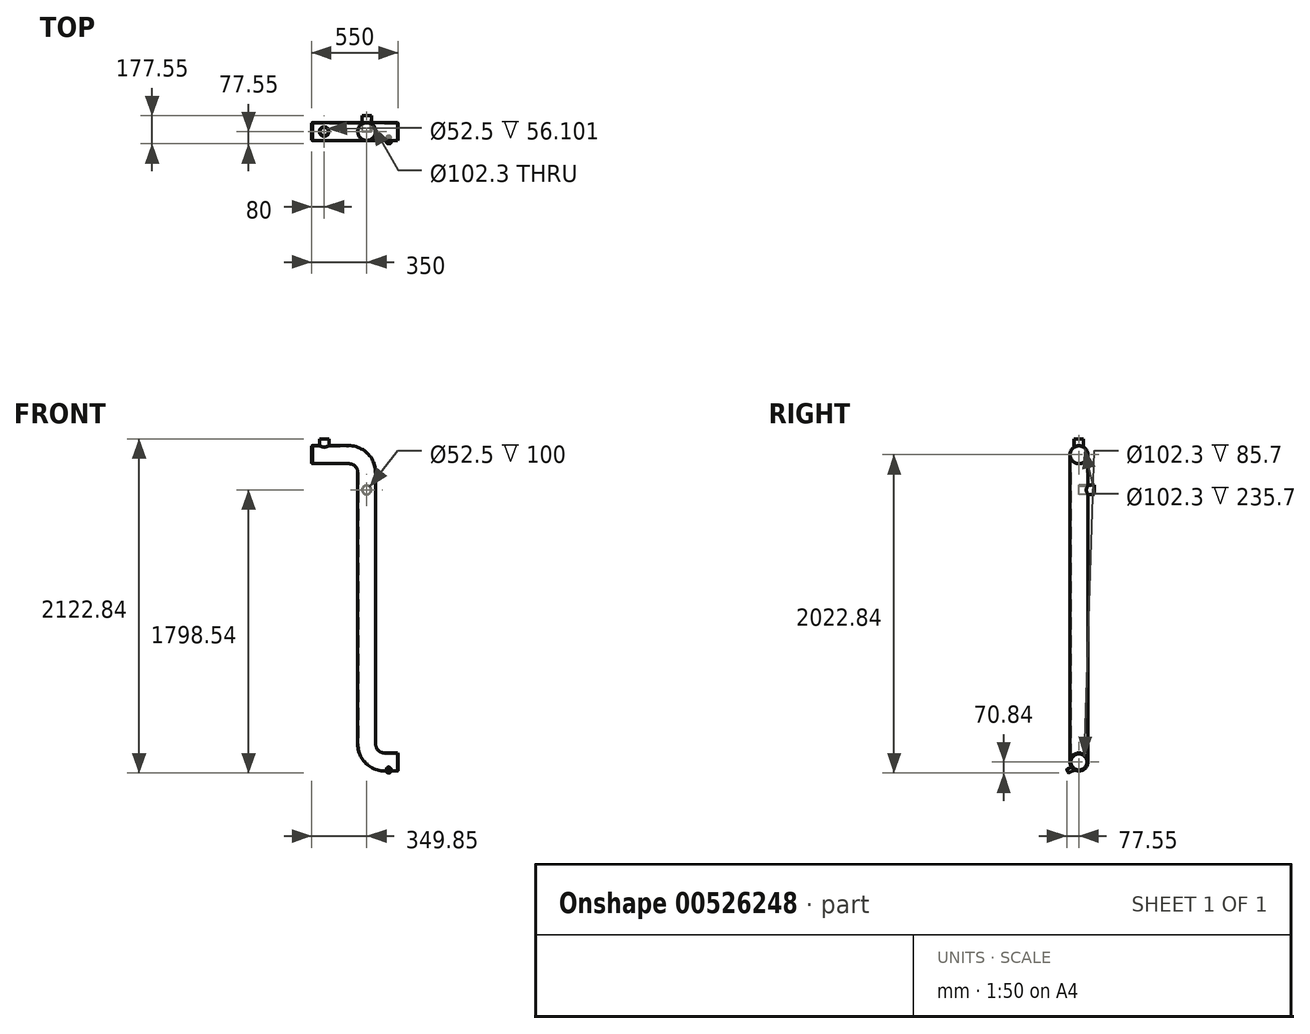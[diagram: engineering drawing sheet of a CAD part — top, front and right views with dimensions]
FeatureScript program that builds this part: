
annotation { "Feature Type Name" : "Feature", "Feature Type Description" : "" }
export const myFeature = defineFeature(function(context is Context, id is Id, definition is map)
    precondition{}
    {
        {
            var Q0;
            Q0=qCreatedBy(makeId("Front.planeOp"),FACE);
            var sketch = newSketch(context, id + "F0", { "sketchPlane" : qUnion([Q0])});
            skLineSegment(sketch, "E0", {"start": v(0, 0) * mm, "end": v(235.7, 0) * mm});
            skLineSegment(sketch, "E1", {"start": v(350, -114.3) * mm, "end": v(350, -1837.7) * mm});
            skLineSegment(sketch, "E2", {"start": v(464.3, -1952) * mm, "end": v(550, -1952) * mm});
            skPoint(sketch, "E3.visualSharp", {"position": v(350, 0) * mm});
            skArc(sketch, "E3.filletArc", {"start": v(350, -114.3) * mm, "mid": v(316.52, -33.48) * mm, "end": v(235.7, 0) * mm});
            skPoint(sketch, "E4.visualSharp", {"position": v(350, -1952) * mm});
            skArc(sketch, "E4.filletArc", {"start": v(350, -1837.7) * mm, "mid": v(383.48, -1918.52) * mm, "end": v(464.3, -1952) * mm});
            skSolve(sketch);
        }
        {
            var Q0;
            Q0=qCreatedBy(makeId("Right.planeOp"),FACE);
            var sketch = newSketch(context, id + "F1", { "sketchPlane" : qUnion([Q0])});
            skCircle(sketch, "E5", {"center": v(0, 0) * mm, "radius": 57.15 * mm});
            skCircle(sketch, "E6", {"center": v(0, 0) * mm, "radius": 51.15 * mm});
            skSolve(sketch);
        }
        {
            var Q0;
            Q0=makeQuery(id+"F1.imprint","IMPRINT",FACE,{"disambiguationData":[TD([[makeQuery(id+"F1.imprint","IMPRINT",EDGE,{"derivedFrom":sQuery(id+"F1.wireOp",EDGE,"E5")}),1.0]])]});
            var Q1;
            Q1=sQuery(id+"F0.wireOp",EDGE,"E0");
            var Q2;
            Q2=sQuery(id+"F0.wireOp",EDGE,"E3.filletArc");
            var Q3;
            Q3=sQuery(id+"F0.wireOp",EDGE,"E1");
            var Q4;
            Q4=sQuery(id+"F0.wireOp",EDGE,"E4.filletArc");
            var Q5;
            Q5=sQuery(id+"F0.wireOp",EDGE,"E2");
            sweep(context, id + "F2", {"profiles" : qUnion([Q0]), "path" : qUnion([Q1, Q2, Q3, Q4, Q5])});
        }
        {
            var Q0;
            Q0=qCreatedBy(makeId("Top.planeOp"),FACE);
            var sketch = newSketch(context, id + "F3", { "sketchPlane" : qUnion([Q0])});
            skCircle(sketch, "E7", {"center": v(80, 0) * mm, "radius": 30.15 * mm});
            skCircle(sketch, "E8", {"center": v(80, 0) * mm, "radius": 26.25 * mm});
            skSolve(sketch);
        }
        {
            var Q0;
            Q0 = qSketchRegion(id + "F3", true);
            extrude(context, id + "F4", {"entities" : qUnion([Q0]), "operationType" : NewBodyOperationType.ADD, "depth" : 100 * mm, "offsetDistance" : 25 * mm});
        }
        {
            var Q0;
            Q0=makeQuery(id+"F4.opExtrude","CAP_FACE",FACE,{"disambiguationData":[OSD([sQuery(id+"F3.wireOp",EDGE,"E7"),sQuery(id+"F3.wireOp",EDGE,"E8")])],"isStart":false});
            var sketch = newSketch(context, id + "F5", { "sketchPlane" : qUnion([Q0])});
            skCircle(sketch, "E9.0", {"center": v(80, 0) * mm, "radius": 26.25 * mm});
            skSolve(sketch);
        }
        {
            var Q0;
            Q0=makeQuery(id+"F5.imprint","IMPRINT",FACE,{"disambiguationData":[TD([[makeQuery(id+"F5.imprint","IMPRINT",EDGE,{"derivedFrom":sQuery(id+"F5.wireOp",EDGE,"E9.0")}),1.0]])]});
            extrude(context, id + "F6", {"entities" : qUnion([Q0]), "operationType" : NewBodyOperationType.REMOVE, "oppositeDirection" : true, "depth" : 100 * mm, "offsetDistance" : 25 * mm});
        }
        {
            var Q0;
            Q0=qCreatedBy(makeId("Right.planeOp"),FACE);
            var sketch = newSketch(context, id + "F7", { "sketchPlane" : qUnion([Q0])});
            skCircle(sketch, "E10.0", {"center": v(0, 0) * mm, "radius": 51.15 * mm});
            skSolve(sketch);
        }
        {
            var Q0;
            Q0=makeQuery(id+"F7.imprint","IMPRINT",FACE,{"disambiguationData":[TD([[makeQuery(id+"F7.imprint","IMPRINT",EDGE,{"derivedFrom":sQuery(id+"F7.wireOp",EDGE,"E10.0")}),1.0]])]});
            extrude(context, id + "F8", {"entities" : qUnion([Q0]), "operationType" : NewBodyOperationType.REMOVE, "depth" : 130 * mm, "offsetDistance" : 25 * mm});
        }
        {
            var Q0;
            Q0=qCreatedBy(makeId("Front.planeOp"),FACE);
            var Q1;
            Q1=makeQuery(id+"F2.opSweep","MID_CAP_EDGE",EDGE,{"disambiguationData":[OSD([sQuery(id+"F0.wireOp",VERTEX,"E2.start"),sQuery(id+"F1.wireOp",EDGE,"E5")])],"capPos":4.0});
            cPlane(context, id + "F9", {"entities" : qUnion([Q0, Q1]), "cplaneType" : CPlaneType.LINE_ANGLE, "offset" : 25 * mm, "angle" : 25 * degree, "width" : 150 * mm, "height" : 150 * mm});
        }
        {
            var Q0;
            Q0=qCreatedBy(id+"F9.planeOp",FACE);
            var sketch = newSketch(context, id + "F10", { "sketchPlane" : qUnion([Q0])});
            skCircle(sketch, "E11", {"center": v(-490, -1791.96) * mm, "radius": 13.35 * mm});
            skCircle(sketch, "E12", {"center": v(-490, -1791.96) * mm, "radius": 10.45 * mm});
            skLineSegment(sketch, "E13", {"start": v(-700, -1711.96) * mm, "end": v(-414.3, -1711.96) * mm});
            skLineSegment(sketch, "E14", {"start": v(-414.3, -1826.26) * mm, "end": v(-700, -1826.26) * mm});
            skSolve(sketch);
        }
        {
            var Q0;
            Q0 = qSketchRegion(id + "F10", true);
            extrude(context, id + "F11", {"entities" : qUnion([Q0]), "operationType" : NewBodyOperationType.ADD, "oppositeDirection" : true, "depth" : 90 * mm, "offsetDistance" : 25 * mm});
        }
        {
            var Q0;
            Q0=makeQuery(id+"F2.opSweep","CAP_FACE",FACE,{"disambiguationData":[OSD([sQuery(id+"F0.wireOp",VERTEX,"E2.end"),sQuery(id+"F1.wireOp",EDGE,"E5"),sQuery(id+"F1.wireOp",EDGE,"E6")])],"isStart":false});
            var sketch = newSketch(context, id + "F12", { "sketchPlane" : qUnion([Q0])});
            skCircle(sketch, "E15.0", {"center": v(0, -1952) * mm, "radius": 51.15 * mm});
            skSolve(sketch);
        }
        {
            var Q0;
            Q0 = qSketchRegion(id + "F12", true);
            extrude(context, id + "F13", {"entities" : qUnion([Q0]), "operationType" : NewBodyOperationType.REMOVE, "oppositeDirection" : true, "depth" : 80 * mm, "offsetDistance" : 25 * mm});
        }
        {
            var Q0;
            Q0=makeQuery(id+"F11.opExtrude","CAP_FACE",FACE,{"disambiguationData":[OSD([sQuery(id+"F10.wireOp",EDGE,"E11"),sQuery(id+"F10.wireOp",EDGE,"E12")])],"isStart":false});
            var sketch = newSketch(context, id + "F14", { "sketchPlane" : qUnion([Q0])});
            skCircle(sketch, "E16.0", {"center": v(490, -1791.96) * mm, "radius": 10.45 * mm});
            skSolve(sketch);
        }
        {
            var Q0;
            Q0 = qSketchRegion(id + "F14", true);
            extrude(context, id + "F15", {"entities" : qUnion([Q0]), "operationType" : NewBodyOperationType.REMOVE, "oppositeDirection" : true, "depth" : 100 * mm, "offsetDistance" : 25 * mm});
        }
        {
            var Q0;
            Q0=makeQuery(id+"F2.opSweep","CAP_EDGE",EDGE,{"disambiguationData":[OSD([sQuery(id+"F0.wireOp",VERTEX,"E0.start"),sQuery(id+"F1.wireOp",EDGE,"E5")])],"isStart":true});
            var Q1;
            Q1=makeQuery(id+"F2.opSweep","CAP_EDGE",EDGE,{"disambiguationData":[OSD([sQuery(id+"F0.wireOp",VERTEX,"E2.end"),sQuery(id+"F1.wireOp",EDGE,"E5")])],"isStart":false});
            chamfer(context, id + "F16", {"entities" : qUnion([Q0, Q1]), "chamferType" : ChamferType.OFFSET_ANGLE, "width" : 5 * mm, "oppositeDirection" : false, "angle" : 30 * degree, "tangentPropagation" : true});
        }
        {
            var Q0;
            Q0=qCreatedBy(makeId("Front.planeOp"),FACE);
            var sketch = newSketch(context, id + "F17", { "sketchPlane" : qUnion([Q0])});
            skLineSegment(sketch, "E17", {"start": v(292.85, -1837.7) * mm, "end": v(292.85, -114.3) * mm});
            skLineSegment(sketch, "E18", {"start": v(407.15, -114.3) * mm, "end": v(407.15, -1837.7) * mm});
            skCircle(sketch, "E19", {"center": v(349.85, -224.3) * mm, "radius": 30.15 * mm});
            skSolve(sketch);
        }
        {
            var Q0;
            Q0 = qSketchRegion(id + "F17", true);
            extrude(context, id + "F18", {"entities" : qUnion([Q0]), "operationType" : NewBodyOperationType.ADD, "oppositeDirection" : true, "depth" : 100 * mm, "offsetDistance" : 25 * mm});
        }
        {
            var Q0;
            Q0=makeQuery(id+"F18.opExtrude","CAP_FACE",FACE,{"disambiguationData":[OSD([sQuery(id+"F17.wireOp",EDGE,"E19")])],"isStart":false});
            var sketch = newSketch(context, id + "F19", { "sketchPlane" : qUnion([Q0])});
            skCircle(sketch, "E20", {"center": v(-349.85, -224.3) * mm, "radius": 26.25 * mm});
            skSolve(sketch);
        }
        {
            var Q0;
            Q0=makeQuery(id+"F19.imprint","IMPRINT",FACE,{"disambiguationData":[TD([[makeQuery(id+"F19.imprint","IMPRINT",EDGE,{"derivedFrom":sQuery(id+"F19.wireOp",EDGE,"E20")}),1.0]])]});
            extrude(context, id + "F20", {"entities" : qUnion([Q0]), "operationType" : NewBodyOperationType.REMOVE, "oppositeDirection" : true, "depth" : 120 * mm, "offsetDistance" : 25 * mm});
        }
    });
